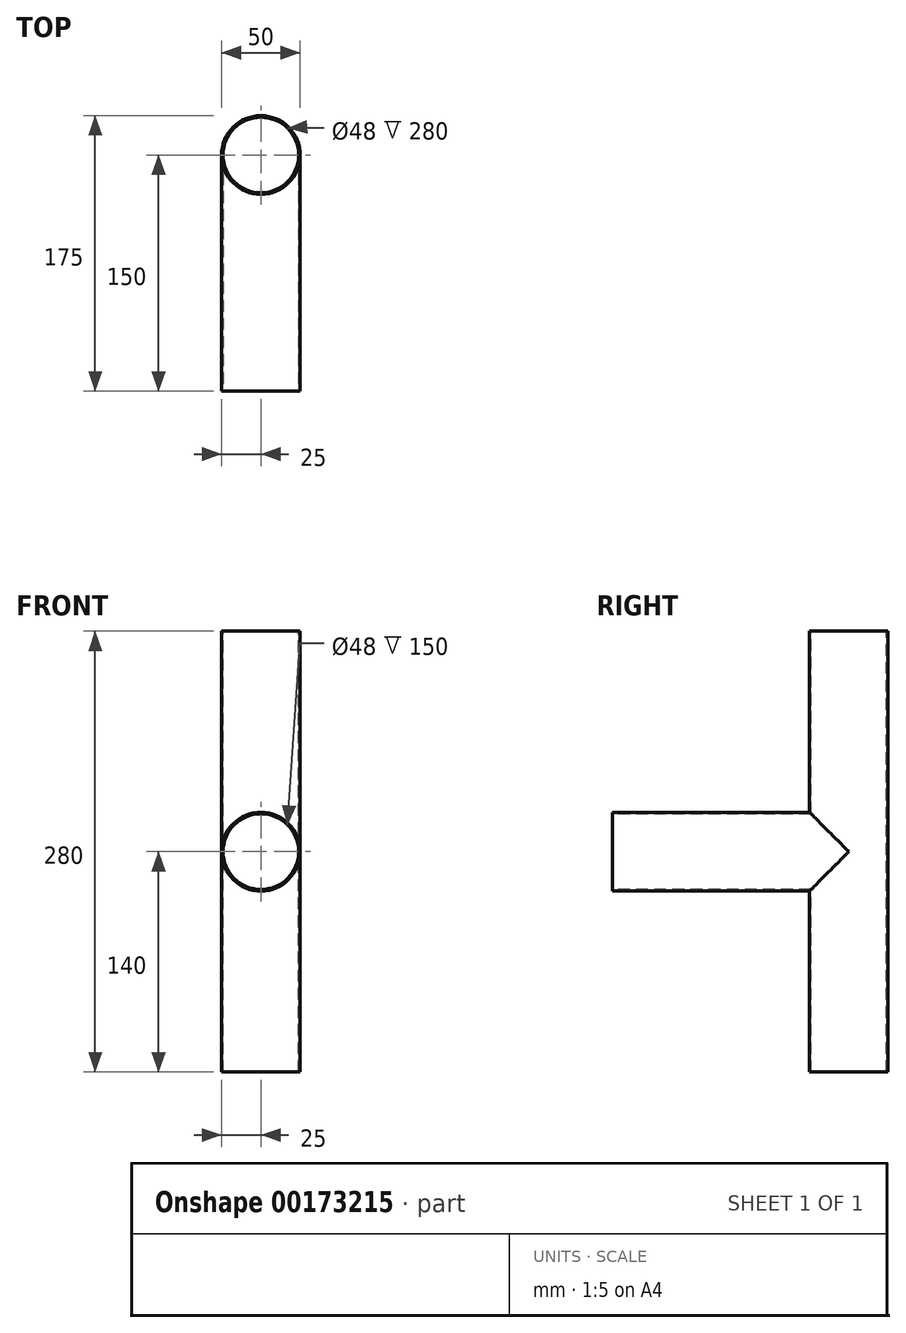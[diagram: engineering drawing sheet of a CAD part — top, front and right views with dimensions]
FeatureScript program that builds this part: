
annotation { "Feature Type Name" : "Feature", "Feature Type Description" : "" }
export const myFeature = defineFeature(function(context is Context, id is Id, definition is map)
    precondition{}
    {
        {
            var Q0;
            Q0=qCreatedBy(makeId("Top.planeOp"),FACE);
            var sketch = newSketch(context, id + "F2", { "sketchPlane" : qUnion([Q0])});
            skCircle(sketch, "E0", {"center": v(0, 0) * mm, "radius": 25 * mm});
            skSolve(sketch);
        }
        {
            var Q0;
            Q0=makeQuery(id+"F2.imprint","IMPRINT",FACE,{"disambiguationData":[TD([[makeQuery(id+"F2.imprint","IMPRINT",EDGE,{"derivedFrom":sQuery(id+"F2.wireOp",EDGE,"E0")}),1.0]])]});
            extrude(context, id + "F3", {"entities" : qUnion([Q0]), "depth" : 280 * mm});
        }
        {
            var Q0;
            Q0=makeQuery(id+"F3.opExtrude","CAP_FACE",FACE,{"disambiguationData":[OSD([sQuery(id+"F2.wireOp",EDGE,"E0")])],"isStart":false});
            var sketch = newSketch(context, id + "F4", { "sketchPlane" : qUnion([Q0])});
            skCircle(sketch, "E1", {"center": v(0, 0) * mm, "radius": 24 * mm});
            skSolve(sketch);
        }
        {
            var Q0;
            Q0=makeQuery(id+"F4.imprint","IMPRINT",FACE,{"disambiguationData":[TD([[makeQuery(id+"F4.imprint","IMPRINT",EDGE,{"derivedFrom":sQuery(id+"F4.wireOp",EDGE,"E1")}),1.0]])]});
            extrude(context, id + "F5", {"entities" : qUnion([Q0]), "operationType" : NewBodyOperationType.REMOVE, "endBound" : BoundingType.THROUGH_ALL, "oppositeDirection" : true, "depth" : 25 * mm});
        }
        {
            var Q0;
            Q0=qCreatedBy(makeId("Front.planeOp"),FACE);
            cPlane(context, id + "F0", {"entities" : qUnion([Q0]), "cplaneType" : CPlaneType.OFFSET, "offset" : 150 * mm, "width" : 150 * mm, "height" : 150 * mm});
        }
        {
            var Q0;
            Q0=qCreatedBy(id+"F0.planeOp",FACE);
            var sketch = newSketch(context, id + "F6", { "sketchPlane" : qUnion([Q0])});
            skLineSegment(sketch, "E2.0", {"start": v(-25, 280) * mm, "end": v(25, 280) * mm});
            skLineSegment(sketch, "E3", {"start": v(-25, 0) * mm, "end": v(-25, 280) * mm});
            skLineSegment(sketch, "E4", {"start": v(25, 280) * mm, "end": v(25, 0) * mm});
            skPoint(sketch, "E5", {"position": v(0, 140) * mm});
            skPoint(sketch, "E6", {"position": v(25, 140) * mm});
            skPoint(sketch, "E7", {"position": v(-25, 140) * mm});
            skCircle(sketch, "E8", {"center": v(0, 140) * mm, "radius": 25 * mm});
            skSolve(sketch);
        }
        {
            var Q0;
            {var subQ0=sQuery(id+"F6.wireOp",EDGE,"E8");var subQ1=makeQuery(id+"F6.imprint","INTERSECT",VERTEX,{"derivedFrom":[sQuery(id+"F6.wireOp",EDGE,"E3"),subQ0]});Q0=makeQuery(id+"F6.imprint","IMPRINT",FACE,{"disambiguationData":[TD([[makeQuery(id+"F6.imprint","IMPRINT",EDGE,{"disambiguationData":[TD([[subQ1,1.0]])],"derivedFrom":subQ0}),1.0]])]});}
            extrude(context, id + "F7", {"entities" : qUnion([Q0]), "operationType" : NewBodyOperationType.ADD, "endBound" : BoundingType.UP_TO_NEXT, "oppositeDirection" : true, "depth" : 25 * mm});
        }
        {
            var Q0;
            Q0=makeQuery(id+"F7.opExtrude","CAP_FACE",FACE,{"disambiguationData":[OSD([sQuery(id+"F6.wireOp",EDGE,"E8")])],"isStart":true});
            var sketch = newSketch(context, id + "F1", { "sketchPlane" : qUnion([Q0])});
            skCircle(sketch, "E9", {"center": v(0, 140) * mm, "radius": 24 * mm});
            skSolve(sketch);
        }
        {
            var Q0;
            Q0=makeQuery(id+"F1.imprint","IMPRINT",FACE,{"disambiguationData":[TD([[makeQuery(id+"F1.imprint","IMPRINT",EDGE,{"derivedFrom":sQuery(id+"F1.wireOp",EDGE,"E9")}),1.0]])]});
            var Q1;
            Q1=makeQuery(id+"F3.opExtrude","SWEPT_BODY",BODY,{"disambiguationData":[OSD([sQuery(id+"F2.wireOp",EDGE,"E0")])]});
            extrude(context, id + "F8", {"entities" : qUnion([Q0]), "operationType" : NewBodyOperationType.REMOVE, "endBound" : BoundingType.UP_TO_BODY, "oppositeDirection" : true, "endBoundEntityBody" : qUnion([Q1]), "depth" : 25 * mm});
        }
    });
